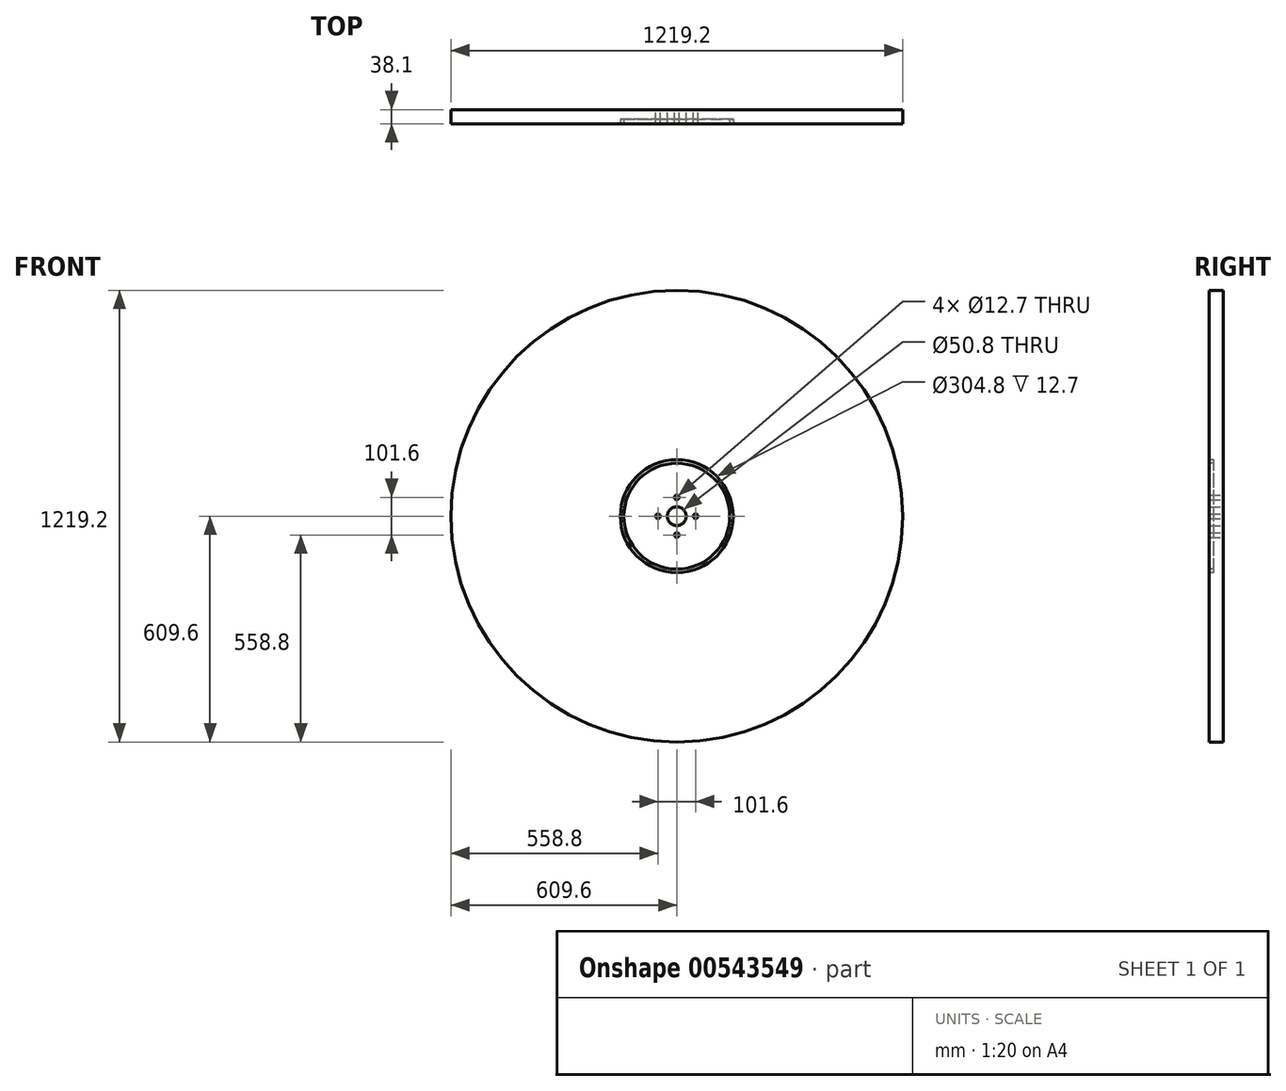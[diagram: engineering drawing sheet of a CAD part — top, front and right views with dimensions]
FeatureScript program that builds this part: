
annotation { "Feature Type Name" : "Feature", "Feature Type Description" : "" }
export const myFeature = defineFeature(function(context is Context, id is Id, definition is map)
    precondition{}
    {
        {
            var Q0;
            Q0=qCreatedBy(makeId("Front.planeOp"),FACE);
            var sketch = newSketch(context, id + "F0", { "sketchPlane" : qUnion([Q0])});
            skCircle(sketch, "E0", {"center": v(0, 0) * mm, "radius": 609.6 * mm});
            skCircle(sketch, "E1", {"center": v(0, 0) * mm, "radius": 25.4 * mm});
            skCircle(sketch, "E2", {"center": v(0, 50.8) * mm, "radius": 6.35 * mm});
            skCircle(sketch, "E3", {"center": v(50.8, 0) * mm, "radius": 6.35 * mm});
            skCircle(sketch, "E4", {"center": v(0, -50.8) * mm, "radius": 6.35 * mm});
            skCircle(sketch, "E5", {"center": v(-50.8, 0) * mm, "radius": 6.35 * mm});
            skSolve(sketch);
        }
        {
            var Q0;
            Q0=makeQuery(id+"F0.imprint","IMPRINT",FACE,{"disambiguationData":[TD([[makeQuery(id+"F0.imprint","IMPRINT",EDGE,{"derivedFrom":sQuery(id+"F0.wireOp",EDGE,"E0")}),1.0]])]});
            extrude(context, id + "F1", {"entities" : qUnion([Q0]), "endBound" : BoundingType.SYMMETRIC, "depth" : 38.1 * mm, "offsetDistance" : 25.4 * mm});
        }
        {
            var Q0;
            Q0=makeQuery(id+"F1.opExtrude","CAP_FACE",FACE,{"disambiguationData":[OSD([sQuery(id+"F0.wireOp",EDGE,"E0"),sQuery(id+"F0.wireOp",EDGE,"E1"),sQuery(id+"F0.wireOp",EDGE,"E2"),sQuery(id+"F0.wireOp",EDGE,"E3"),sQuery(id+"F0.wireOp",EDGE,"E4"),sQuery(id+"F0.wireOp",EDGE,"E5")])],"isStart":false});
            var sketch = newSketch(context, id + "F2", { "sketchPlane" : qUnion([Q0])});
            skCircle(sketch, "E6", {"center": v(0, 0) * mm, "radius": 142.88 * mm});
            skCircle(sketch, "E7", {"center": v(0, 0) * mm, "radius": 152.4 * mm});
            skSolve(sketch);
        }
        {
            var Q0;
            Q0=makeQuery(id+"F2.imprint","IMPRINT",FACE,{"disambiguationData":[TD([[makeQuery(id+"F2.imprint","IMPRINT",EDGE,{"derivedFrom":sQuery(id+"F2.wireOp",EDGE,"E6")}),-1.0]])]});
            extrude(context, id + "F3", {"entities" : qUnion([Q0]), "operationType" : NewBodyOperationType.REMOVE, "oppositeDirection" : true, "depth" : 12.7 * mm, "offsetDistance" : 25.4 * mm});
        }
    });
